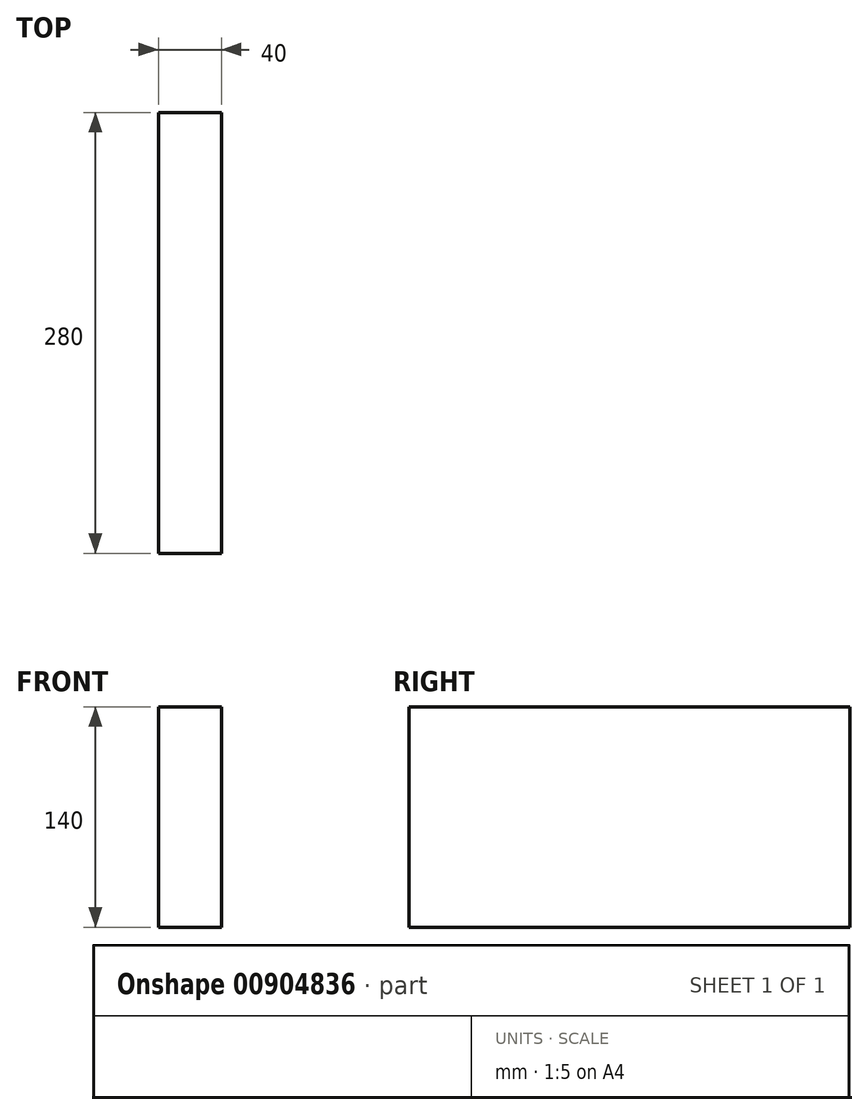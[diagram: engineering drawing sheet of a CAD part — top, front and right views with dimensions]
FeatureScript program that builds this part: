
annotation { "Feature Type Name" : "Feature", "Feature Type Description" : "" }
export const myFeature = defineFeature(function(context is Context, id is Id, definition is map)
    precondition{}
    {
        {
            var Q0;
            Q0=qCreatedBy(makeId("Front.planeOp"),FACE);
            var sketch = newSketch(context, id + "F0", { "sketchPlane" : qUnion([Q0])});
            skLineSegment(sketch, "E0.bottom", {"start": v(20, -70) * mm, "end": v(-20, -70) * mm});
            skLineSegment(sketch, "E0.top", {"start": v(20, 70) * mm, "end": v(-20, 70) * mm});
            skLineSegment(sketch, "E0.left", {"start": v(20, -70) * mm, "end": v(20, 70) * mm});
            skLineSegment(sketch, "E0.right", {"start": v(-20, -70) * mm, "end": v(-20, 70) * mm});
            skPoint(sketch, "E0.middle", {"position": v(0, 0) * mm});
            skSolve(sketch);
        }
        {
            var Q0;
            Q0=makeQuery(id+"F0.imprint","IMPRINT",FACE,{"disambiguationData":[TD([[makeQuery(id+"F0.imprint","IMPRINT",EDGE,{"derivedFrom":sQuery(id+"F0.wireOp",EDGE,"E0.bottom")}),-1.0]])]});
            extrude(context, id + "F1", {"entities" : qUnion([Q0]), "depth" : 280 * mm, "offsetDistance" : 25.4 * mm});
        }
    });
